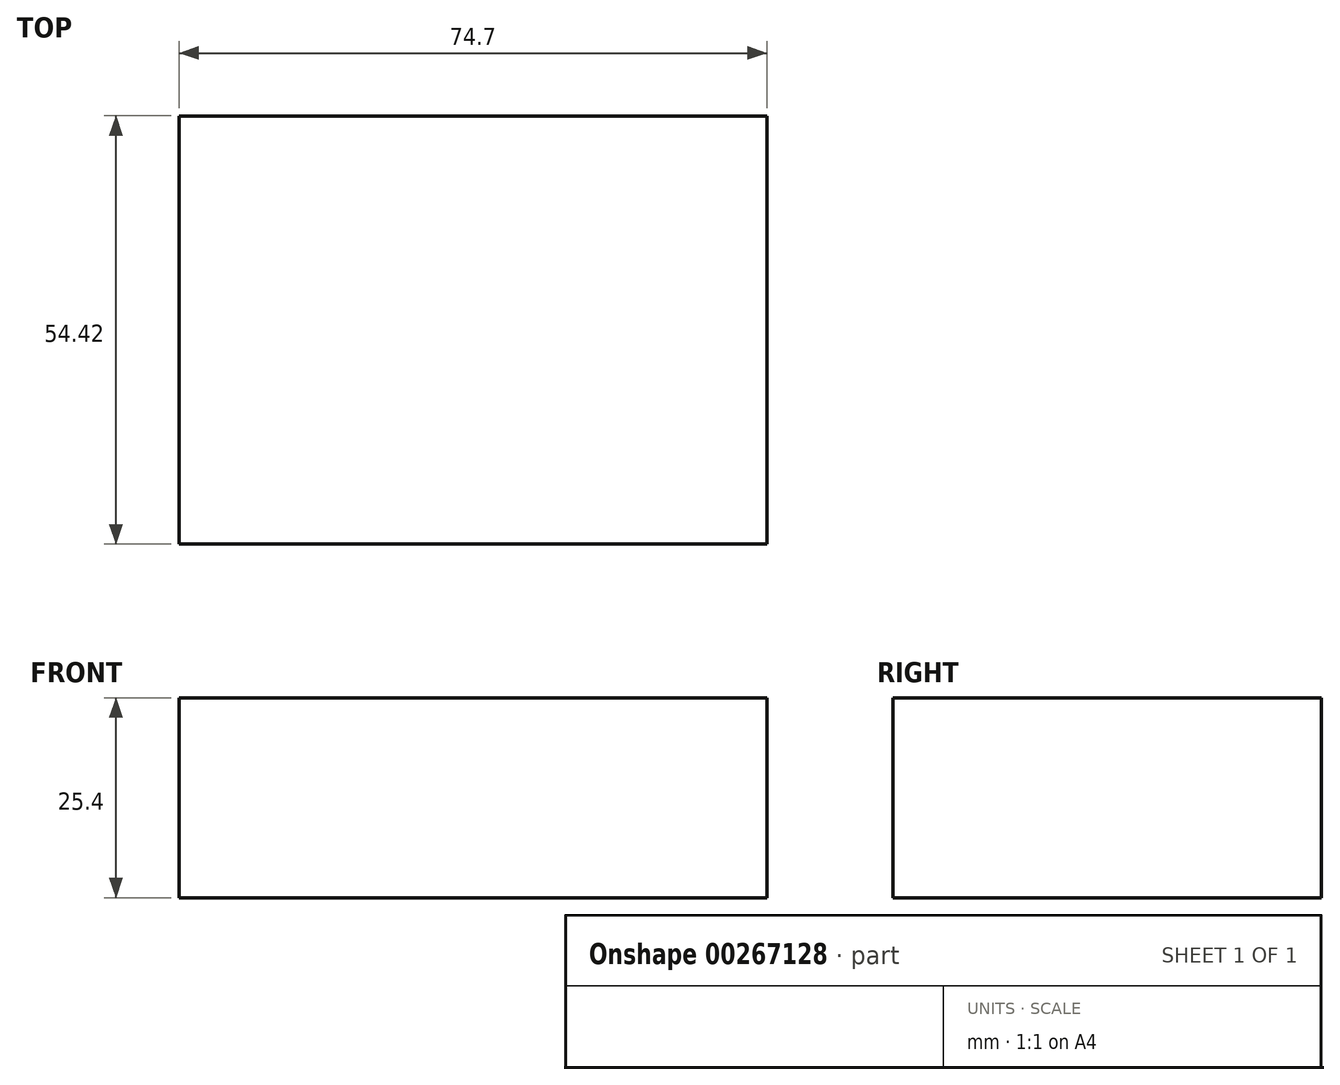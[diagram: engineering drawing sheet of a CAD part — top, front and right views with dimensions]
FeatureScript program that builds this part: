
annotation { "Feature Type Name" : "Feature", "Feature Type Description" : "" }
export const myFeature = defineFeature(function(context is Context, id is Id, definition is map)
    precondition{}
    {
        {
            var Q0;
            Q0=qCreatedBy(makeId("Top.planeOp"),FACE);
            var sketch = newSketch(context, id + "F0", { "sketchPlane" : qUnion([Q0])});
            skLineSegment(sketch, "E0.bottom", {"start": v(-56.88, 43.42) * mm, "end": v(17.82, 43.42) * mm});
            skLineSegment(sketch, "E0.top", {"start": v(-56.88, -11) * mm, "end": v(17.82, -11) * mm});
            skLineSegment(sketch, "E0.left", {"start": v(-56.88, 43.42) * mm, "end": v(-56.88, -11) * mm});
            skLineSegment(sketch, "E0.right", {"start": v(17.82, 43.42) * mm, "end": v(17.82, -11) * mm});
            skSolve(sketch);
        }
        {
            var Q0;
            Q0 = qSketchRegion(id + "F0", true);
            extrude(context, id + "F1", {"entities" : qUnion([Q0]), "depth" : 25.4 * mm});
        }
    });
